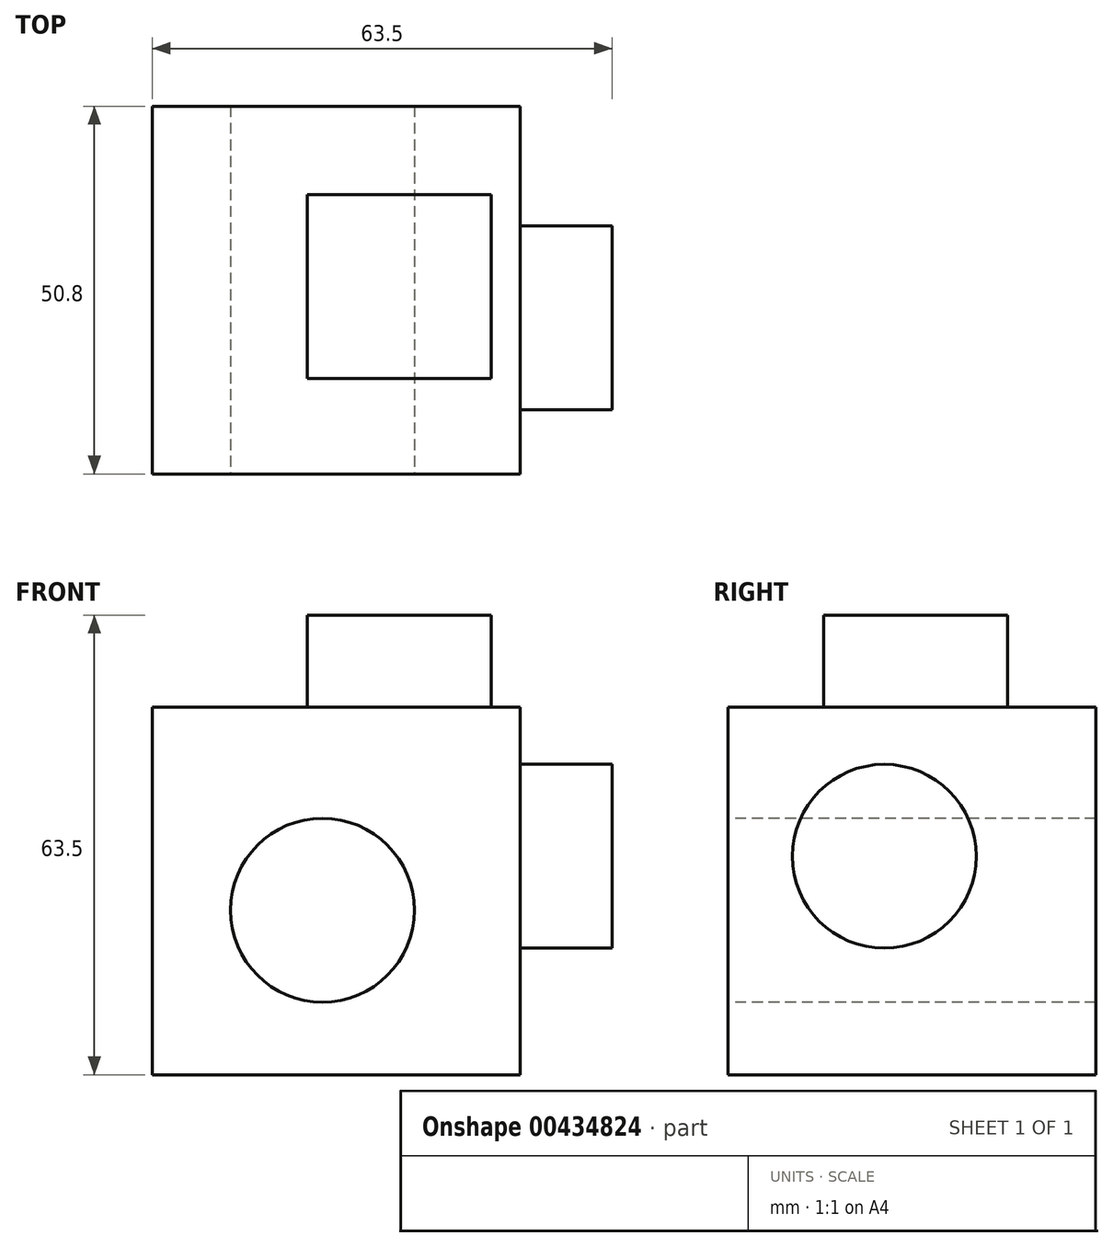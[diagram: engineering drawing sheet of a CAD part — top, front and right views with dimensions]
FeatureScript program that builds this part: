
annotation { "Feature Type Name" : "Feature", "Feature Type Description" : "" }
export const myFeature = defineFeature(function(context is Context, id is Id, definition is map)
    precondition{}
    {
        {
            var Q0;
            Q0=qCreatedBy(makeId("Front.planeOp"),FACE);
            var sketch = newSketch(context, id + "F0", { "sketchPlane" : qUnion([Q0])});
            skLineSegment(sketch, "E0", {"start": v(-50.8, 0) * mm, "end": v(0, 0) * mm});
            skLineSegment(sketch, "E1", {"start": v(0, 0) * mm, "end": v(0, 50.8) * mm});
            skLineSegment(sketch, "E2", {"start": v(0, 50.8) * mm, "end": v(-50.8, 50.8) * mm});
            skLineSegment(sketch, "E3", {"start": v(-50.8, 50.8) * mm, "end": v(-50.8, 0) * mm});
            skSolve(sketch);
        }
        {
            var Q0;
            Q0 = qSketchRegion(id + "F0", true);
            extrude(context, id + "F1", {"entities" : qUnion([Q0]), "depth" : 50.8 * mm});
        }
        {
            var Q0;
            Q0=makeQuery(id+"F1.opExtrude","CAP_FACE",FACE,{"disambiguationData":[OSD([sQuery(id+"F0.wireOp",EDGE,"E0"),sQuery(id+"F0.wireOp",EDGE,"E1"),sQuery(id+"F0.wireOp",EDGE,"E2"),sQuery(id+"F0.wireOp",EDGE,"E3")])],"isStart":false});
            var sketch = newSketch(context, id + "F2", { "sketchPlane" : qUnion([Q0])});
            skCircle(sketch, "E4", {"center": v(-27.3, 22.72) * mm, "radius": 12.7 * mm});
            skSolve(sketch);
        }
        {
            var Q0;
            Q0 = qSketchRegion(id + "F2", true);
            extrude(context, id + "F3", {"entities" : qUnion([Q0]), "operationType" : NewBodyOperationType.REMOVE, "oppositeDirection" : true, "depth" : 50.8 * mm});
        }
        {
            var Q0;
            Q0=makeQuery(id+"F1.opExtrude","SWEPT_FACE",FACE,{"disambiguationData":[OSD([sQuery(id+"F0.wireOp",EDGE,"E1")])]});
            var sketch = newSketch(context, id + "F4", { "sketchPlane" : qUnion([Q0])});
            skCircle(sketch, "E5", {"center": v(-29.22, 30.17) * mm, "radius": 12.7 * mm});
            skSolve(sketch);
        }
        {
            var Q0;
            Q0 = qSketchRegion(id + "F4", true);
            extrude(context, id + "F5", {"entities" : qUnion([Q0]), "operationType" : NewBodyOperationType.ADD, "depth" : 12.7 * mm});
        }
        {
            var Q0;
            Q0=makeQuery(id+"F1.opExtrude","SWEPT_FACE",FACE,{"disambiguationData":[OSD([sQuery(id+"F0.wireOp",EDGE,"E2")])]});
            var sketch = newSketch(context, id + "F6", { "sketchPlane" : qUnion([Q0])});
            skLineSegment(sketch, "E6.bottom", {"start": v(-29.41, -12.22) * mm, "end": v(-4.01, -12.22) * mm});
            skLineSegment(sketch, "E6.top", {"start": v(-29.41, -37.62) * mm, "end": v(-4.01, -37.62) * mm});
            skLineSegment(sketch, "E6.left", {"start": v(-29.41, -12.22) * mm, "end": v(-29.41, -37.62) * mm});
            skLineSegment(sketch, "E6.right", {"start": v(-4.01, -12.22) * mm, "end": v(-4.01, -37.62) * mm});
            skSolve(sketch);
        }
        {
            var Q0;
            Q0 = qSketchRegion(id + "F6", true);
            extrude(context, id + "F7", {"entities" : qUnion([Q0]), "operationType" : NewBodyOperationType.ADD, "depth" : 12.7 * mm});
        }
    });
